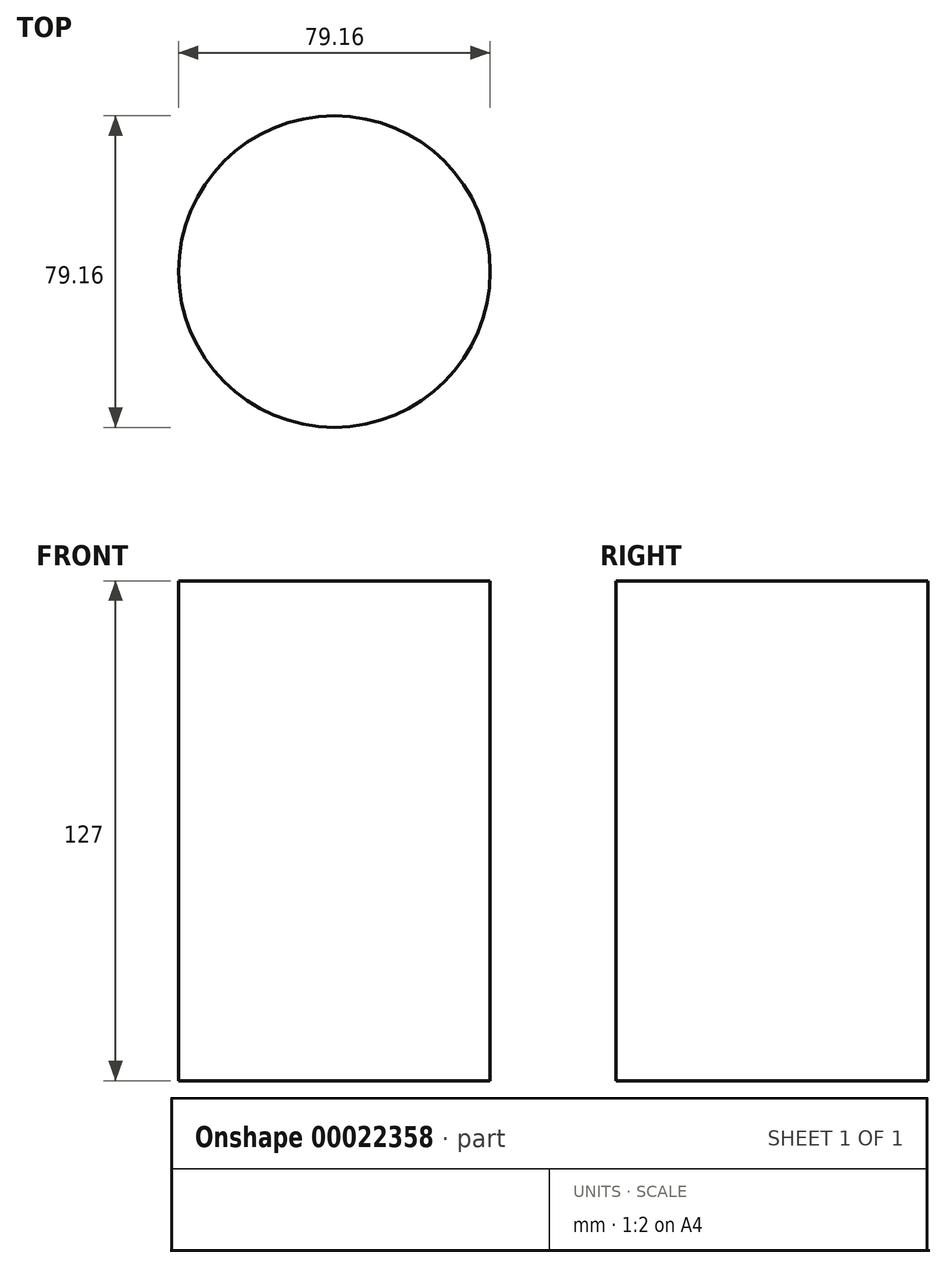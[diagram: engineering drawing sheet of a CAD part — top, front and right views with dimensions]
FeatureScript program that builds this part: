
annotation { "Feature Type Name" : "Feature", "Feature Type Description" : "" }
export const myFeature = defineFeature(function(context is Context, id is Id, definition is map)
    precondition{}
    {
        {
            var Q0;
            Q0=qCreatedBy(makeId("Top.planeOp"),FACE);
            var sketch = newSketch(context, id + "F0", { "sketchPlane" : qUnion([Q0])});
            skCircle(sketch, "E0", {"center": v(0, 0) * mm, "radius": 39.58 * mm});
            skSolve(sketch);
        }
        {
            var Q0;
            Q0=makeQuery(id+"F0.imprint","IMPRINT",FACE,{"disambiguationData":[TD([[makeQuery(id+"F0.imprint","IMPRINT",EDGE,{"derivedFrom":sQuery(id+"F0.wireOp",EDGE,"E0")}),1.0]])]});
            extrude(context, id + "F1", {"entities" : qUnion([Q0]), "depth" : 127 * mm});
        }
    });
